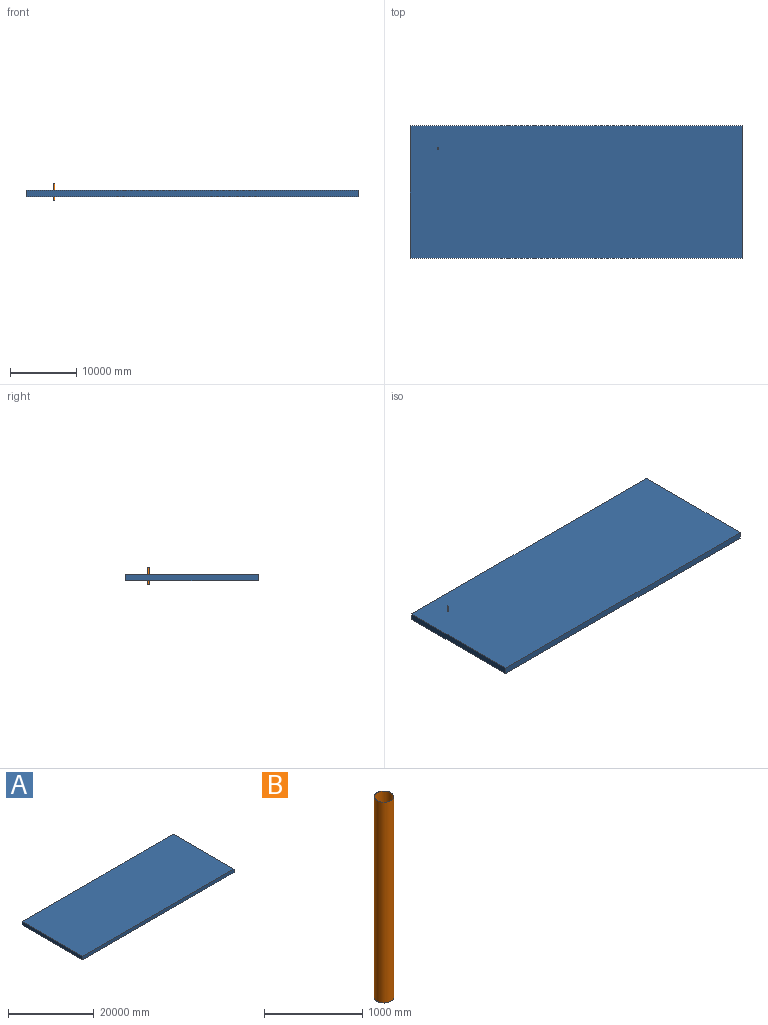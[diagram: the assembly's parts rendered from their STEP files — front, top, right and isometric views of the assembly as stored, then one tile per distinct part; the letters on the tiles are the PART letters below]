
ASSEMBLY  parts=2 mates=1
PART A: 6 faces, bbox 50000x20000x1000 mm
  f0: plane 50000x1000mm, normal (0,1,0), area 50000000mm2, adj f1,f3,f4,f5
  f1: plane 20000x1000mm, normal (-1,0,0), area 20000000mm2, adj f0,f2,f4,f5
  f2: plane 50000x1000mm, normal (0,-1,0), area 50000000mm2, adj f1,f3,f4,f5
  f3: plane 20000x1000mm, normal (1,0,0), area 20000000mm2, adj f0,f2,f4,f5
  f4: plane 50000x20000mm, normal (0,0,-1), area 1000000000mm2, adj f0,f1,f2,f3
  f5: plane 50000x20000mm, normal (0,0,1), area 1000000000mm2, adj f0,f1,f2,f3
PART B: 4 faces, bbox 200x200x2500 mm
  f0: cylinder r=100mm len=2500mm, axis (0,0,-1), area 1570796.3mm2, adj f1,f2
  f1: plane 200x200mm, normal (0,0,1), area 1551.2mm2, adj f0,f3
  f2: plane 200x200mm, normal (0,0,-1), area 1551.2mm2, adj f0,f3
  f3: cylinder r=97.5mm len=2500mm, axis (0,0,-1), area 1531526.4mm2, adj f1,f2
PLACE A t=(-33090.24,15072.37,-21737.26)mm fixed
PLACE B rot(axis=(0,0,1),132.7deg) t=(-28850.79,11628.82,-23237.26)mm
MATE planar A.f5 <-> B.f0  axis (0,0,1) through (-8090.24,5072.37,-21737.26)mm
